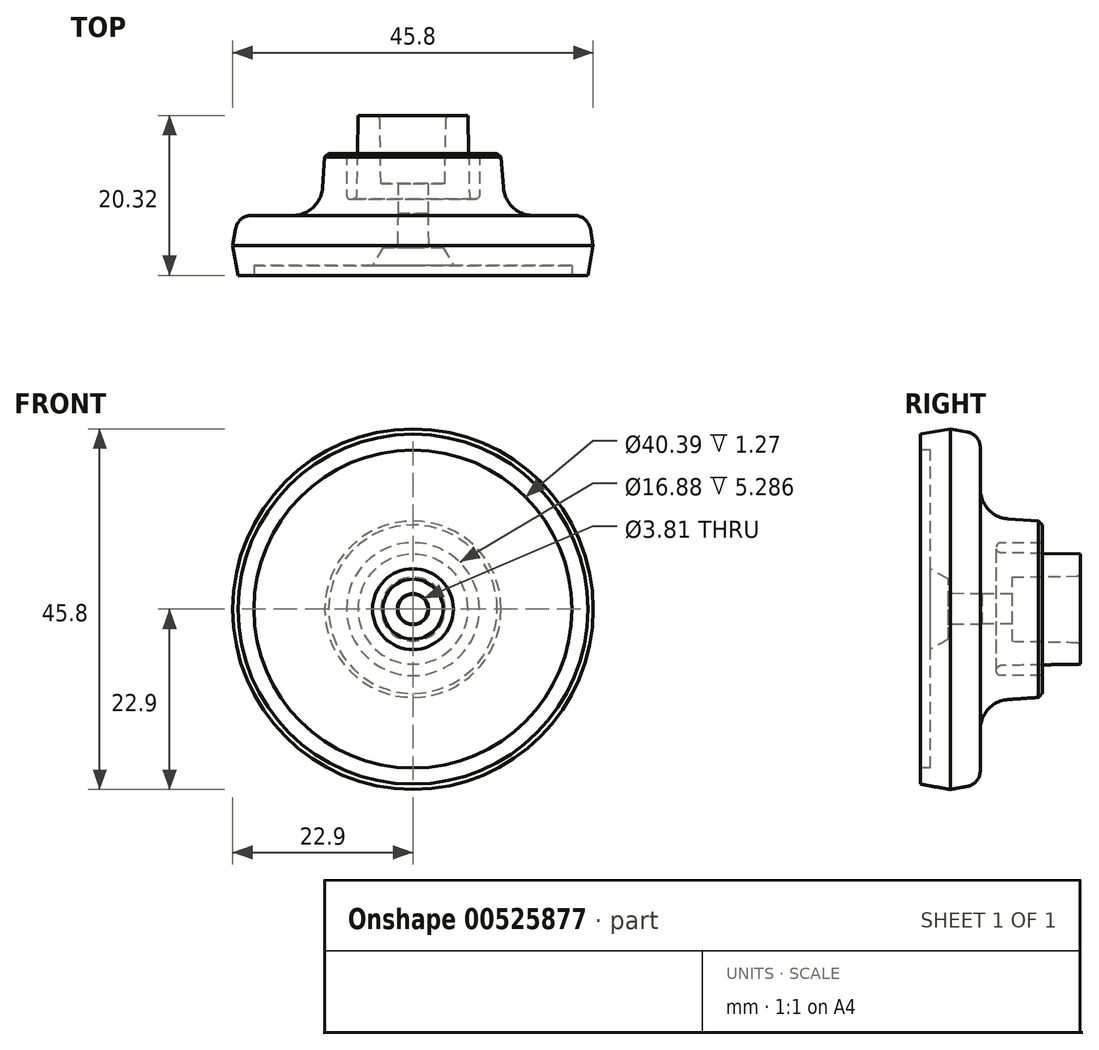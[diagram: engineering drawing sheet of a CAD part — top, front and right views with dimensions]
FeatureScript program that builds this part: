
annotation { "Feature Type Name" : "Feature", "Feature Type Description" : "" }
export const myFeature = defineFeature(function(context is Context, id is Id, definition is map)
    precondition{}
    {
        {
            var Q0;
            Q0=qCreatedBy(makeId("Top.planeOp"),FACE);
            var sketch = newSketch(context, id + "F0", { "sketchPlane" : qUnion([Q0])});
            skLineSegment(sketch, "E0", {"start": v(1.9, 11.68) * mm, "end": v(4.06, 11.68) * mm});
            skLineSegment(sketch, "E1", {"start": v(4.21, 20.32) * mm, "end": v(6.99, 20.32) * mm});
            skLineSegment(sketch, "E2", {"start": v(8.44, 15.5) * mm, "end": v(11.18, 15.5) * mm});
            skLineSegment(sketch, "E3", {"start": v(11.73, 7.62) * mm, "end": v(22.22, 7.62) * mm});
            skLineSegment(sketch, "E4", {"start": v(22.23, 0) * mm, "end": v(20.2, 0) * mm});
            skLineSegment(sketch, "E5", {"start": v(20.2, 0) * mm, "end": v(20.2, 1.27) * mm});
            skLineSegment(sketch, "E6", {"start": v(20.2, 1.27) * mm, "end": v(5.13, 1.27) * mm});
            skLineSegment(sketch, "E7", {"start": v(22.9, 3.8) * mm, "end": v(22.22, 7.62) * mm});
            skLineSegment(sketch, "E8", {"start": v(22.9, 3.81) * mm, "end": v(22.23, 0) * mm});
            skLineSegment(sketch, "E9", {"start": v(11.73, 7.62) * mm, "end": v(11.18, 15.5) * mm});
            skLineSegment(sketch, "E10", {"start": v(4.06, 11.68) * mm, "end": v(4.21, 20.32) * mm});
            skLineSegment(sketch, "E11", {"start": v(1.9, 7.87) * mm, "end": v(1.9, 11.68) * mm});
            skLineSegment(sketch, "E12", {"start": v(0, 0) * mm, "end": v(0, 57.96) * mm, "construction": true});
            skLineSegment(sketch, "E13", {"start": v(1.9, 7.87) * mm, "end": v(1.98, 3.56) * mm});
            skLineSegment(sketch, "E14", {"start": v(1.98, 3.56) * mm, "end": v(3.81, 3.56) * mm});
            skLineSegment(sketch, "E15", {"start": v(3.81, 3.56) * mm, "end": v(5.13, 1.27) * mm});
            skLineSegment(sketch, "E16", {"start": v(7.17, 9.7) * mm, "end": v(8.44, 9.7) * mm});
            skLineSegment(sketch, "E17", {"start": v(8.44, 9.7) * mm, "end": v(8.44, 15.5) * mm});
            skLineSegment(sketch, "E18", {"start": v(6.99, 20.32) * mm, "end": v(7.17, 9.7) * mm});
            skSolve(sketch);
        }
        {
            var Q0;
            Q0=qSketchRegion(id+"F0",true);
            var Q1;
            Q1=sQuery(id+"F0.wireOp",EDGE,"E12");
            revolve(context, id + "F1", {"entities" : qUnion([Q0]), "axis" : qUnion([Q1]), "revolveType" : RevolveType.FULL});
        }
        {
            var Q0;
            Q0=makeQuery(id+"F1.opRevolve","SWEPT_EDGE",EDGE,{"disambiguationData":[OSD([sQuery(id+"F0.wireOp",EDGE,"E3"),sQuery(id+"F0.wireOp",EDGE,"E9")])]});
            fillet(context, id + "F2", {"entities" : qUnion([Q0]), "radius" : 3.8 * mm, "tangentPropagation" : true, "allowEdgeOverflow" : false});
        }
        {
            var Q0;
            Q0=makeQuery(id+"F1.opRevolve","SWEPT_EDGE",EDGE,{"disambiguationData":[OSD([sQuery(id+"F0.wireOp",EDGE,"E3"),sQuery(id+"F0.wireOp",EDGE,"E7")])]});
            fillet(context, id + "F3", {"entities" : qUnion([Q0]), "radius" : 2.03 * mm, "tangentPropagation" : true, "allowEdgeOverflow" : false});
        }
        {
            var Q0;
            Q0=makeQuery(id+"F1.opRevolve","SWEPT_EDGE",EDGE,{"disambiguationData":[OSD([sQuery(id+"F0.wireOp",EDGE,"E16"),sQuery(id+"F0.wireOp",EDGE,"E17")])]});
            var Q1;
            Q1=makeQuery(id+"F1.opRevolve","SWEPT_EDGE",EDGE,{"disambiguationData":[OSD([sQuery(id+"F0.wireOp",EDGE,"cXm76Fhz-yke0-jxkx-pxMH-KzrELMCJ1eQU"),sQuery(id+"F0.wireOp",EDGE,"E16")])]});
            fillet(context, id + "F4", {"entities" : qUnion([Q0, Q1]), "radius" : 0.5 * mm, "tangentPropagation" : true, "allowEdgeOverflow" : false});
        }
        {
            var Q0;
            Q0=makeQuery(id+"F1.opRevolve","SWEPT_EDGE",EDGE,{"disambiguationData":[OSD([sQuery(id+"F0.wireOp",EDGE,"E2"),sQuery(id+"F0.wireOp",EDGE,"E9")])]});
            chamfer(context, id + "F5", {"entities" : qUnion([Q0]), "width" : 0.5 * mm, "tangentPropagation" : true});
        }
        {
            var Q0;
            Q0=makeQuery(id+"F1.opRevolve","SWEPT_EDGE",EDGE,{"disambiguationData":[OSD([sQuery(id+"F0.wireOp",EDGE,"E1"),sQuery(id+"F0.wireOp",EDGE,"E10")])]});
            fillet(context, id + "F6", {"entities" : qUnion([Q0]), "radius" : 0.5 * mm, "tangentPropagation" : true, "allowEdgeOverflow" : false});
        }
    });
